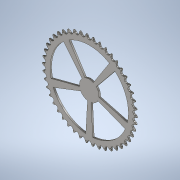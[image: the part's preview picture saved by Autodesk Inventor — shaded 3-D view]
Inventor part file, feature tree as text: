
AUTODESK INVENTOR PART (.ipt)
format: ipt  version: 2021 (Build 250183000, 183)  size: 1,103,360 bytes
history: native  units: mm
features: other x6, extrude x3, pattern_circular x2, pattern_linear x1, sketch x1
ambient origin geometry x8: Origin, YZ Plane, XZ Plane, XY Plane, X Axis, Y Axis, Z Axis, Center Point
bodies: Solid1 (feature_tree)
feature tree (13):
  other  "Theoretical Tooth Profile"
  other  "Tooth Profile"
  other  "Section Profile"
  other  "Shroud"
  other  "Strand"
  pattern_linear  "Strand Pattern"  Spacing1=1.36591mm  [1 undecoded]
  extrude  "Theoretical Tooth"  Depth=20.0mm
  extrude  "Tooth"  Depth=20.0mm
  pattern_circular  "Tooth Pattern"  [2 undecoded]
  other  "Timing Plane"
  extrude  "Extrusion4"  Depth=20.0mm
  pattern_circular  "Circular Pattern2"  [2 undecoded]
  sketch  "Sketch4"  dims[d0=186.101273mm d2=1.36591mm d3=3.91375mm d10=22.044267mm d11=2.929118mm d12=6.2mm d13=10.11375mm d14=10.85mm d18=10.0mm d19=0.0mm d20=460.0mm d21=360.0deg d23=3.81mm d28=0.0mm d29=0.0mm d30=3.069mm d31=166.745028mm d32=3.069mm d33=0.762mm d34=12.7mm d36=90.0deg d37=90.0deg d38=10.0mm d40=13.92mm d42=0.0mm d43=1.5345mm d44=24.093133mm d45=44.64mm d46=3.91375mm d47=10.0mm d48=0.0mm d49=0.0mm d50=10.0mm d51=80.0mm d52=21.118484mm d53=10.821041mm d54=20.0mm d55=20.245819mm d56=8.901179mm d57=0.0mm d58=0.0mm d59=50.0mm d60=360.0deg]
note: 5 required parameter values undecoded (feature->parameter linkage not recoverable at this tier; creation-order binding heuristic only, values carry confidence <= 0.55)
